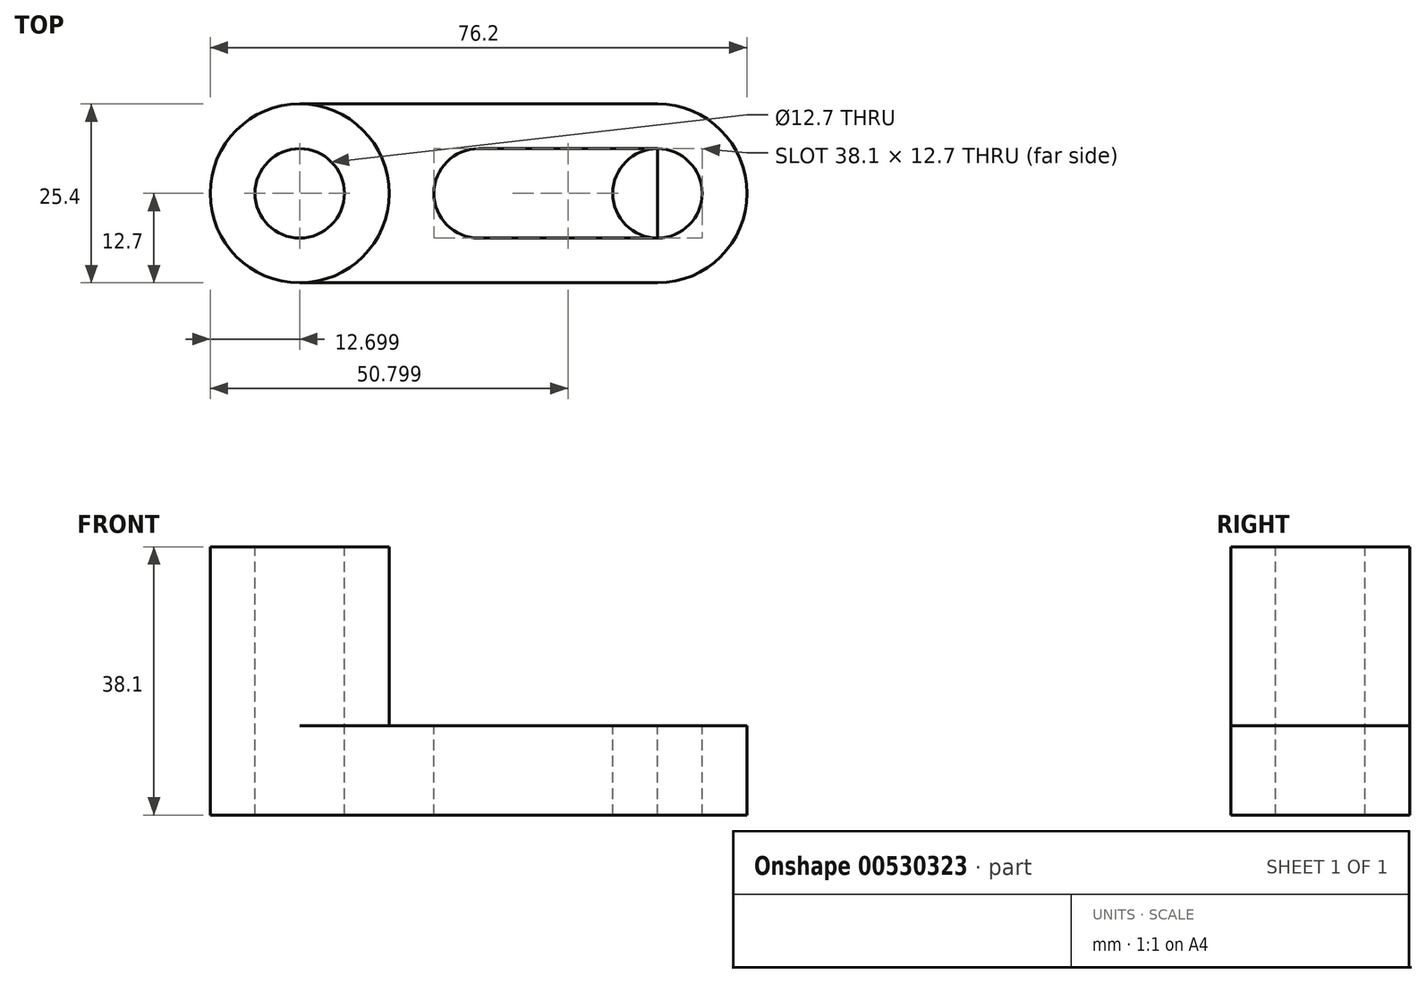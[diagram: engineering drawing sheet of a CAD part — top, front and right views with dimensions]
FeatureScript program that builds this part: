
annotation { "Feature Type Name" : "Feature", "Feature Type Description" : "" }
export const myFeature = defineFeature(function(context is Context, id is Id, definition is map)
    precondition{}
    {
        {
            var Q0;
            Q0=qCreatedBy(makeId("Front.planeOp"),FACE);
            var sketch = newSketch(context, id + "F0", { "sketchPlane" : qUnion([Q0])});
            skLineSegment(sketch, "E0", {"start": v(-65.64, 46.84) * mm, "end": v(-65.64, 8.74) * mm});
            skLineSegment(sketch, "E1", {"start": v(-65.64, 8.74) * mm, "end": v(10.56, 8.74) * mm});
            skLineSegment(sketch, "E2", {"start": v(10.56, 8.74) * mm, "end": v(10.56, 21.44) * mm});
            skLineSegment(sketch, "E3", {"start": v(10.56, 21.44) * mm, "end": v(-40.24, 21.44) * mm});
            skLineSegment(sketch, "E4", {"start": v(-40.24, 21.44) * mm, "end": v(-40.24, 46.84) * mm});
            skLineSegment(sketch, "E5", {"start": v(-65.64, 46.84) * mm, "end": v(-40.24, 46.84) * mm});
            skSolve(sketch);
        }
        {
            var Q0;
            Q0=makeQuery(id+"F0.imprint","IMPRINT",FACE,{"disambiguationData":[TD([[makeQuery(id+"F0.imprint","IMPRINT",EDGE,{"derivedFrom":sQuery(id+"F0.wireOp",EDGE,"E0")}),1.0]])]});
            extrude(context, id + "F1", {"entities" : qUnion([Q0]), "depth" : 25.4 * mm, "offsetDistance" : 25.4 * mm});
        }
        {
            var Q0;
            Q0=makeQuery(id+"F1.opExtrude","SWEPT_FACE",FACE,{"disambiguationData":[OSD([sQuery(id+"F0.wireOp",EDGE,"E5")])]});
            var sketch = newSketch(context, id + "F2", { "sketchPlane" : qUnion([Q0])});
            skCircle(sketch, "E6", {"center": v(-52.94, -12.7) * mm, "radius": 12.7 * mm});
            skPoint(sketch, "E6.centerSnap0", {"position": v(-52.94, 0) * mm});
            skSolve(sketch);
        }
        {
            var Q0;
            {var subQ0=sQuery(id+"F2.wireOp",EDGE,"E6");var subQ1=sQuery(id+"F0.wireOp",EDGE,"E5");var subQ2=makeQuery(id+"F1.opExtrude","CAP_EDGE",EDGE,{"disambiguationData":[OSD([subQ1])],"isStart":true});var subQ3=makeQuery(id+"F2.imprint","INTERSECT",VERTEX,{"derivedFrom":[subQ2,subQ0]});Q0=makeQuery(id+"F2.imprint","IMPRINT",FACE,{"disambiguationData":[TD([[makeQuery(id+"F2.imprint","IMPRINT",EDGE,{"disambiguationData":[TD([[subQ3,-1.0]])],"derivedFrom":subQ0}),-1.0]])]});}
            var Q1;
            {var subQ0=sQuery(id+"F2.wireOp",EDGE,"E6");var subQ1=sQuery(id+"F0.wireOp",EDGE,"E5");var subQ2=makeQuery(id+"F1.opExtrude","CAP_EDGE",EDGE,{"disambiguationData":[OSD([subQ1])],"isStart":true});var subQ3=makeQuery(id+"F2.imprint","INTERSECT",VERTEX,{"derivedFrom":[subQ2,subQ0]});Q1=makeQuery(id+"F2.imprint","IMPRINT",FACE,{"disambiguationData":[TD([[makeQuery(id+"F2.imprint","IMPRINT",EDGE,{"disambiguationData":[TD([[subQ3,1.0]])],"derivedFrom":subQ0}),-1.0]])]});}
            var Q2;
            {var subQ0=sQuery(id+"F2.wireOp",EDGE,"E6");var subQ1=sQuery(id+"F0.wireOp",EDGE,"E5");var subQ4=makeQuery(id+"F1.opExtrude","CAP_EDGE",EDGE,{"disambiguationData":[OSD([subQ1])],"isStart":false});var subQ5=makeQuery(id+"F2.imprint","INTERSECT",VERTEX,{"derivedFrom":[subQ4,subQ0]});Q2=makeQuery(id+"F2.imprint","IMPRINT",FACE,{"disambiguationData":[TD([[makeQuery(id+"F2.imprint","IMPRINT",EDGE,{"disambiguationData":[TD([[subQ5,-1.0]])],"derivedFrom":subQ0}),-1.0]])]});}
            var Q3;
            {var subQ0=sQuery(id+"F2.wireOp",EDGE,"E6");var subQ1=sQuery(id+"F0.wireOp",EDGE,"E5");var subQ4=makeQuery(id+"F1.opExtrude","CAP_EDGE",EDGE,{"disambiguationData":[OSD([subQ1])],"isStart":false});var subQ5=makeQuery(id+"F2.imprint","INTERSECT",VERTEX,{"derivedFrom":[subQ4,subQ0]});Q3=makeQuery(id+"F2.imprint","IMPRINT",FACE,{"disambiguationData":[TD([[makeQuery(id+"F2.imprint","IMPRINT",EDGE,{"disambiguationData":[TD([[subQ5,1.0]])],"derivedFrom":subQ0}),-1.0]])]});}
            extrude(context, id + "F3", {"entities" : qUnion([Q0, Q1, Q2, Q3]), "operationType" : NewBodyOperationType.REMOVE, "oppositeDirection" : true, "depth" : 25.4 * mm, "offsetDistance" : 25.4 * mm});
        }
        {
            var Q0;
            {var subQ0=sQuery(id+"F0.wireOp",EDGE,"E5");var subQ1=makeQuery(id+"F1.opExtrude","CAP_EDGE",EDGE,{"disambiguationData":[OSD([subQ0])],"isStart":true});var subQ2=sQuery(id+"F0.wireOp",EDGE,"E0");var subQ3=makeQuery(id+"F1.opExtrude","SWEPT_EDGE",EDGE,{"disambiguationData":[OSD([subQ2,subQ0])]});var subQ4=makeQuery(id+"F2.imprint","INTERSECT",VERTEX,{"derivedFrom":[subQ3,subQ1]});var subQ5=sQuery(id+"F2.wireOp",EDGE,"E6");var subQ6=makeQuery(id+"F2.imprint","INTERSECT",VERTEX,{"derivedFrom":[subQ1,subQ5]});Q0=makeQuery(id+"F3.boolean.opBoolean","COPY",FACE,{"derivedFrom":makeQuery(id+"F3.opExtrude","CAP_FACE",FACE,{"disambiguationData":[OSD([subQ2,subQ0,subQ5]),TDD([makeQuery(id+"F2.imprint","IMPRINT",EDGE,{"disambiguationData":[TD([[subQ6,-1.0]])],"derivedFrom":subQ5}),makeQuery(id+"F2.imprint","IMPRINT",EDGE,{"disambiguationData":[TD([[subQ4,1.0]])],"derivedFrom":subQ3}),makeQuery(id+"F2.imprint","IMPRINT",EDGE,{"disambiguationData":[TD([[subQ6,1.0]])],"derivedFrom":subQ1})])],"isStart":false})});}
            var Q1;
            {var subQ0=sQuery(id+"F0.wireOp",EDGE,"E5");var subQ1=makeQuery(id+"F1.opExtrude","CAP_EDGE",EDGE,{"disambiguationData":[OSD([subQ0])],"isStart":false});var subQ2=sQuery(id+"F0.wireOp",EDGE,"E0");var subQ3=makeQuery(id+"F1.opExtrude","SWEPT_EDGE",EDGE,{"disambiguationData":[OSD([subQ2,subQ0])]});var subQ4=makeQuery(id+"F2.imprint","INTERSECT",VERTEX,{"derivedFrom":[subQ3,subQ1]});var subQ5=sQuery(id+"F2.wireOp",EDGE,"E6");var subQ6=makeQuery(id+"F2.imprint","INTERSECT",VERTEX,{"derivedFrom":[subQ1,subQ5]});Q1=makeQuery(id+"F3.boolean.opBoolean","COPY",FACE,{"derivedFrom":makeQuery(id+"F3.opExtrude","CAP_FACE",FACE,{"disambiguationData":[OSD([subQ2,subQ0,subQ5]),TDD([makeQuery(id+"F2.imprint","IMPRINT",EDGE,{"disambiguationData":[TD([[subQ6,1.0]])],"derivedFrom":subQ5}),makeQuery(id+"F2.imprint","IMPRINT",EDGE,{"disambiguationData":[TD([[subQ4,-1.0]])],"derivedFrom":subQ3}),makeQuery(id+"F2.imprint","IMPRINT",EDGE,{"disambiguationData":[TD([[subQ6,1.0]])],"derivedFrom":subQ1})])],"isStart":false})});}
            extrude(context, id + "F4", {"entities" : qUnion([Q0, Q1]), "operationType" : NewBodyOperationType.REMOVE, "oppositeDirection" : true, "depth" : 25.4 * mm, "offsetDistance" : 25.4 * mm});
        }
        {
            var Q0;
            {var subQ0=sQuery(id+"F0.wireOp",EDGE,"E5");var subQ1=makeQuery(id+"F1.opExtrude","CAP_EDGE",EDGE,{"disambiguationData":[OSD([subQ0])],"isStart":false});var subQ2=sQuery(id+"F0.wireOp",EDGE,"E4");var subQ3=makeQuery(id+"F1.opExtrude","SWEPT_EDGE",EDGE,{"disambiguationData":[OSD([subQ2,subQ0])]});var subQ4=makeQuery(id+"F2.imprint","INTERSECT",VERTEX,{"derivedFrom":[subQ3,subQ1]});var subQ5=sQuery(id+"F2.wireOp",EDGE,"E6");var subQ6=makeQuery(id+"F2.imprint","INTERSECT",VERTEX,{"derivedFrom":[subQ1,subQ5]});var subQ8=makeQuery(id+"F1.opExtrude","CAP_EDGE",EDGE,{"disambiguationData":[OSD([subQ0])],"isStart":true});var subQ9=makeQuery(id+"F2.imprint","INTERSECT",VERTEX,{"derivedFrom":[subQ3,subQ8]});var subQ10=makeQuery(id+"F2.imprint","INTERSECT",VERTEX,{"derivedFrom":[subQ8,subQ5]});Q0=makeQuery(id+"F3.boolean.opBoolean","MERGE",FACE,{"derivedFrom":[makeQuery(id+"F1.opExtrude","SWEPT_FACE",FACE,{"disambiguationData":[OSD([sQuery(id+"F0.wireOp",EDGE,"E3")])]}),makeQuery(id+"F3.opExtrude","CAP_FACE",FACE,{"disambiguationData":[OSD([subQ2,subQ0,subQ5]),TDD([makeQuery(id+"F2.imprint","IMPRINT",EDGE,{"disambiguationData":[TD([[subQ10,1.0]])],"derivedFrom":subQ5}),makeQuery(id+"F2.imprint","IMPRINT",EDGE,{"disambiguationData":[TD([[subQ9,1.0]])],"derivedFrom":subQ3}),makeQuery(id+"F2.imprint","IMPRINT",EDGE,{"disambiguationData":[TD([[subQ10,-1.0]])],"derivedFrom":subQ8})])],"isStart":false}),makeQuery(id+"F3.opExtrude","CAP_FACE",FACE,{"disambiguationData":[OSD([subQ2,subQ0,subQ5]),TDD([makeQuery(id+"F2.imprint","IMPRINT",EDGE,{"disambiguationData":[TD([[subQ6,-1.0]])],"derivedFrom":subQ5}),makeQuery(id+"F2.imprint","IMPRINT",EDGE,{"disambiguationData":[TD([[subQ4,-1.0]])],"derivedFrom":subQ3}),makeQuery(id+"F2.imprint","IMPRINT",EDGE,{"disambiguationData":[TD([[subQ6,-1.0]])],"derivedFrom":subQ1})])],"isStart":false})]});}
            var sketch = newSketch(context, id + "F5", { "sketchPlane" : qUnion([Q0])});
            skCircle(sketch, "E7", {"center": v(-2.14, -12.7) * mm, "radius": 6.35 * mm});
            skCircle(sketch, "E8", {"center": v(-27.54, -12.7) * mm, "radius": 6.35 * mm});
            skLineSegment(sketch, "E9", {"start": v(-27.54, -12.7) * mm, "end": v(-27.54, -19.05) * mm});
            skLineSegment(sketch, "E10", {"start": v(-27.54, -19.05) * mm, "end": v(-27.54, -6.35) * mm});
            skLineSegment(sketch, "E11", {"start": v(-27.54, -6.35) * mm, "end": v(-2.14, -6.35) * mm});
            skLineSegment(sketch, "E12", {"start": v(-27.54, -19.05) * mm, "end": v(-2.14, -19.05) * mm});
            skLineSegment(sketch, "E13", {"start": v(-2.14, -12.7) * mm, "end": v(-2.14, 0) * mm});
            skLineSegment(sketch, "E14", {"start": v(-2.14, 0) * mm, "end": v(-2.14, -25.4) * mm});
            skLineSegment(sketch, "E15", {"start": v(-2.14, -12.7) * mm, "end": v(10.56, -12.7) * mm});
            skArc(sketch, "E16", {"start": v(-2.14, -25.4) * mm, "mid": v(10.56, -12.7) * mm, "end": v(-2.14, 0) * mm});
            skSolve(sketch);
        }
        {
            var Q0;
            {var subQ0=sQuery(id+"F5.wireOp",EDGE,"E10");var subQ4=makeQuery(id+"F5.imprint","IMPRINT",VERTEX,{"derivedFrom":subQ0});Q0=makeQuery(id+"F5.imprint","IMPRINT",FACE,{"disambiguationData":[TD([[makeQuery(id+"F5.imprint","IMPRINT",EDGE,{"disambiguationData":[TD([[subQ4,1.0]])],"derivedFrom":subQ0}),1.0]])]});}
            var Q1;
            {var subQ0=sQuery(id+"F5.wireOp",EDGE,"E10");var subQ4=makeQuery(id+"F5.imprint","IMPRINT",VERTEX,{"derivedFrom":subQ0});Q1=makeQuery(id+"F5.imprint","IMPRINT",FACE,{"disambiguationData":[TD([[makeQuery(id+"F5.imprint","IMPRINT",EDGE,{"disambiguationData":[TD([[subQ4,1.0]])],"derivedFrom":subQ0}),-1.0]])]});}
            var Q2;
            {var subQ1=sQuery(id+"F5.wireOp",EDGE,"E11");Q2=makeQuery(id+"F5.imprint","IMPRINT",FACE,{"disambiguationData":[TD([[makeQuery(id+"F5.imprint","IMPRINT",EDGE,{"derivedFrom":subQ1}),-1.0]])]});}
            var Q3;
            {var subQ0=sQuery(id+"F5.wireOp",EDGE,"E14");var subQ4=makeQuery(id+"F5.imprint","INTERSECT",VERTEX,{"derivedFrom":[subQ0,sQuery(id+"F5.wireOp",EDGE,"E15")]});Q3=makeQuery(id+"F5.imprint","IMPRINT",FACE,{"disambiguationData":[TD([[makeQuery(id+"F5.imprint","IMPRINT",EDGE,{"disambiguationData":[TD([[subQ4,1.0]])],"derivedFrom":subQ0}),-1.0]])]});}
            var Q4;
            {var subQ0=sQuery(id+"F5.wireOp",EDGE,"E14");var subQ3=sQuery(id+"F5.wireOp",EDGE,"E15");var subQ5=makeQuery(id+"F5.imprint","INTERSECT",VERTEX,{"derivedFrom":[subQ0,subQ3]});Q4=makeQuery(id+"F5.imprint","IMPRINT",FACE,{"disambiguationData":[TD([[makeQuery(id+"F5.imprint","IMPRINT",EDGE,{"disambiguationData":[TD([[subQ5,-1.0]])],"derivedFrom":subQ3}),-1.0]])]});}
            var Q5;
            {var subQ0=sQuery(id+"F5.wireOp",EDGE,"E14");var subQ3=sQuery(id+"F5.wireOp",EDGE,"E15");var subQ5=makeQuery(id+"F5.imprint","INTERSECT",VERTEX,{"derivedFrom":[subQ0,subQ3]});Q5=makeQuery(id+"F5.imprint","IMPRINT",FACE,{"disambiguationData":[TD([[makeQuery(id+"F5.imprint","IMPRINT",EDGE,{"disambiguationData":[TD([[subQ5,-1.0]])],"derivedFrom":subQ3}),1.0]])]});}
            var Q6;
            {var subQ0=sQuery(id+"F5.wireOp",EDGE,"E16");var subQ3=sQuery(id+"F0.wireOp",EDGE,"E3");var subQ6=makeQuery(id+"F1.opExtrude","SWEPT_EDGE",EDGE,{"disambiguationData":[OSD([sQuery(id+"F0.wireOp",EDGE,"E2"),subQ3])]});var subQ7=makeQuery(id+"F5.imprint","INTERSECT",VERTEX,{"derivedFrom":[subQ6,sQuery(id+"F5.wireOp",EDGE,"E15"),subQ0]});Q6=makeQuery(id+"F5.imprint","IMPRINT",FACE,{"disambiguationData":[TD([[makeQuery(id+"F5.imprint","IMPRINT",EDGE,{"disambiguationData":[TD([[subQ7,-1.0]])],"derivedFrom":subQ0}),-1.0]])]});}
            var Q7;
            {var subQ0=sQuery(id+"F5.wireOp",EDGE,"E16");var subQ3=sQuery(id+"F0.wireOp",EDGE,"E3");var subQ6=makeQuery(id+"F1.opExtrude","SWEPT_EDGE",EDGE,{"disambiguationData":[OSD([sQuery(id+"F0.wireOp",EDGE,"E2"),subQ3])]});var subQ7=makeQuery(id+"F5.imprint","INTERSECT",VERTEX,{"derivedFrom":[subQ6,sQuery(id+"F5.wireOp",EDGE,"E15"),subQ0]});Q7=makeQuery(id+"F5.imprint","IMPRINT",FACE,{"disambiguationData":[TD([[makeQuery(id+"F5.imprint","IMPRINT",EDGE,{"disambiguationData":[TD([[subQ7,1.0]])],"derivedFrom":subQ0}),-1.0]])]});}
            extrude(context, id + "F6", {"entities" : qUnion([Q0, Q1, Q2, Q3, Q4, Q5, Q6, Q7]), "operationType" : NewBodyOperationType.REMOVE, "endBound" : BoundingType.THROUGH_ALL, "oppositeDirection" : true, "depth" : 25.4 * mm, "offsetDistance" : 25.4 * mm});
        }
        {
            var Q0;
            Q0=makeQuery(id+"F1.opExtrude","SWEPT_FACE",FACE,{"disambiguationData":[OSD([sQuery(id+"F0.wireOp",EDGE,"E5")])]});
            var sketch = newSketch(context, id + "F7", { "sketchPlane" : qUnion([Q0])});
            skCircle(sketch, "E17", {"center": v(-52.94, -12.7) * mm, "radius": 6.35 * mm});
            skSolve(sketch);
        }
        {
            var Q0;
            Q0=makeQuery(id+"F7.imprint","IMPRINT",FACE,{"disambiguationData":[TD([[makeQuery(id+"F7.imprint","IMPRINT",EDGE,{"derivedFrom":sQuery(id+"F7.wireOp",EDGE,"E17")}),1.0]])]});
            extrude(context, id + "F8", {"entities" : qUnion([Q0]), "operationType" : NewBodyOperationType.REMOVE, "endBound" : BoundingType.THROUGH_ALL, "oppositeDirection" : true, "depth" : 25.4 * mm, "offsetDistance" : 25.4 * mm});
        }
    });
